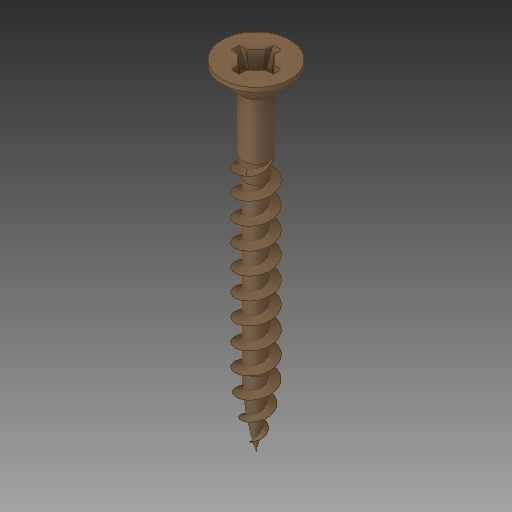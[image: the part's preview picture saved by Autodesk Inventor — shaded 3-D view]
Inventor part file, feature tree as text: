
AUTODESK INVENTOR PART (.ipt)
format: ipt  version: 2018 (Build 220112000, 112)  size: 716,288 bytes
history: native  units: in
note: dims shown in document units (in); Inventor stores cm internally (conversion verified against a paired STEP export)
features: other x1, thread x1
ambient origin geometry x8: Origin, YZ Plane, XZ Plane, XY Plane, X Axis, Y Axis, Z Axis, Center Point
bodies: Solid1 (feature_tree), Solid2 (feature_tree)
feature tree (2):
  parser-record x1  (decoder bookkeeping rows leaked as tree rows — omitted from the tree; the rows remain in map.json)
  thread  "Thread-1"  [1 undecoded]
note: 1 required parameter value undecoded (feature->parameter linkage not recoverable at this tier; creation-order binding heuristic only, values carry confidence <= 0.55)
